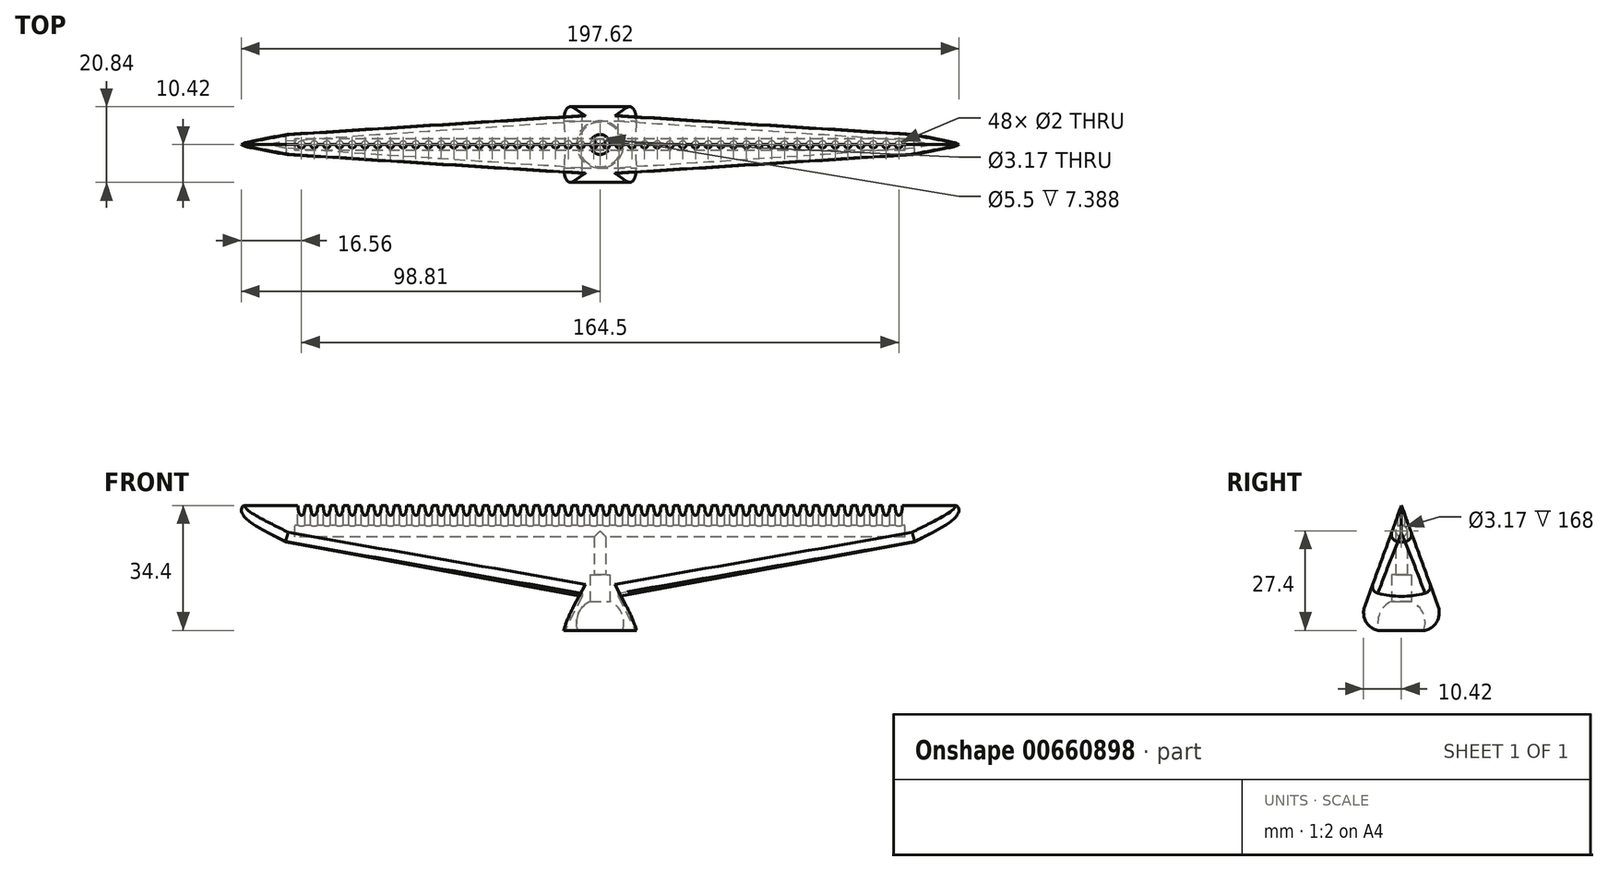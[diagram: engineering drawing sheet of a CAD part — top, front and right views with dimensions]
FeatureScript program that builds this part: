
annotation { "Feature Type Name" : "Feature", "Feature Type Description" : "" }
export const myFeature = defineFeature(function(context is Context, id is Id, definition is map)
    precondition{}
    {
        {
            var Q0;
            Q0=qCreatedBy(makeId("Front.planeOp"),FACE);
            var sketch = newSketch(context, id + "F0", { "sketchPlane" : qUnion([Q0])});
            skLineSegment(sketch, "E0.MirrorCS", {"start": v(10, 0) * mm, "end": v(5, 10) * mm});
            skLineSegment(sketch, "E1.MirrorCS", {"start": v(86.5, 25) * mm, "end": v(5, 10) * mm});
            skLineSegment(sketch, "E2.MirrorCS", {"start": v(0, 0) * mm, "end": v(10, 0) * mm});
            skLineSegment(sketch, "E3", {"start": v(0, 35) * mm, "end": v(100, 35) * mm});
            skPoint(sketch, "E4.end.orphan", {"position": v(0, 30) * mm});
            skArc(sketch, "E5", {"start": v(99.82, 31.74) * mm, "mid": v(100.91, 33.31) * mm, "end": v(100, 35) * mm});
            skPoint(sketch, "E5.second.point", {"position": v(98.3, 31.76) * mm});
            skPoint(sketch, "E5.third.point", {"position": v(100, 31.83) * mm});
            skLineSegment(sketch, "E6", {"start": v(86.5, 25) * mm, "end": v(100, 31.83) * mm});
            skArc(sketch, "E7.MirrorCS", {"start": v(-99.82, 31.74) * mm, "mid": v(-100.91, 33.31) * mm, "end": v(-100, 35) * mm});
            skLineSegment(sketch, "E8.MirrorCS", {"start": v(0, 35) * mm, "end": v(-100, 35) * mm});
            skLineSegment(sketch, "E9.MirrorCS", {"start": v(0, 0) * mm, "end": v(-10, 0) * mm});
            skPoint(sketch, "E10.MirrorP", {"position": v(-100, 31.83) * mm});
            skLineSegment(sketch, "E11.MirrorCS", {"start": v(-86.5, 25) * mm, "end": v(-5, 10) * mm});
            skLineSegment(sketch, "E12.MirrorCS", {"start": v(-10, 0) * mm, "end": v(-5, 10) * mm});
            skPoint(sketch, "E13.MirrorP", {"position": v(-98.3, 31.76) * mm});
            skLineSegment(sketch, "E14.MirrorCS", {"start": v(-86.5, 25) * mm, "end": v(-100, 31.83) * mm});
            skPoint(sketch, "E15.orphan", {"position": v(0, 0) * mm});
            skSolve(sketch);
        }
        {
            var Q0;
            Q0=makeQuery(id+"F0.imprint","IMPRINT",FACE,{"disambiguationData":[TD([[makeQuery(id+"F0.imprint","IMPRINT",EDGE,{"derivedFrom":sQuery(id+"F0.wireOp",EDGE,"E0.MirrorCS")}),1.0]])]});
            var Q1;
            Q1=sQuery(id+"F0.wireOp",EDGE,"E8.MirrorCS");
            revolve(context, id + "F1", {"entities" : qUnion([Q0]), "axis" : qUnion([Q1]), "revolveType" : RevolveType.SYMMETRIC, "angle" : 40 * degree});
        }
        {
            var Q0;
            Q0=qCreatedBy(makeId("Right.planeOp"),FACE);
            var sketch = newSketch(context, id + "F2", { "sketchPlane" : qUnion([Q0])});
            skLineSegment(sketch, "E16", {"start": v(0, 0.6) * mm, "end": v(-10, 0.6) * mm});
            skLineSegment(sketch, "E17", {"start": v(0, 0) * mm, "end": v(-10, 0) * mm});
            skLineSegment(sketch, "E18", {"start": v(-10, 0.6) * mm, "end": v(-10, 0) * mm});
            skLineSegment(sketch, "E19.MirrorCS", {"start": v(0, 0.6) * mm, "end": v(10, 0.6) * mm});
            skLineSegment(sketch, "E20.MirrorCS", {"start": v(10, 0.6) * mm, "end": v(10, 0) * mm});
            skLineSegment(sketch, "E21.MirrorCS", {"start": v(0, 0) * mm, "end": v(10, 0) * mm});
            skSolve(sketch);
        }
        {
            var Q0;
            Q0=makeQuery(id+"F2.imprint","IMPRINT",FACE,{"disambiguationData":[TD([[makeQuery(id+"F2.imprint","IMPRINT",EDGE,{"derivedFrom":sQuery(id+"F2.wireOp",EDGE,"E16")}),1.0]])]});
            extrude(context, id + "F3", {"entities" : qUnion([Q0]), "operationType" : NewBodyOperationType.REMOVE, "endBound" : BoundingType.SYMMETRIC, "depth" : 20 * mm, "offsetDistance" : 25 * mm});
        }
        {
            var Q0;
            Q0=qCreatedBy(makeId("Front.planeOp"),FACE);
            var sketch = newSketch(context, id + "F4", { "sketchPlane" : qUnion([Q0])});
            skLineSegment(sketch, "E22", {"start": v(0, 0) * mm, "end": v(0, 1.02) * mm});
            skLineSegment(sketch, "E23", {"start": v(0, 1.02) * mm, "end": v(0, 2.72) * mm});
            skArc(sketch, "E24", {"start": v(0, 9.22) * mm, "mid": v(-6.5, 2.72) * mm, "end": v(0, -3.78) * mm});
            skLineSegment(sketch, "E25", {"start": v(0, 0) * mm, "end": v(0, -3.78) * mm});
            skLineSegment(sketch, "E26", {"start": v(0, 2.72) * mm, "end": v(0, 9.22) * mm});
            skSolve(sketch);
        }
        {
            var Q0;
            Q0=makeQuery(id+"F4.imprint","IMPRINT",FACE,{"disambiguationData":[TD([[makeQuery(id+"F4.imprint","IMPRINT",EDGE,{"derivedFrom":sQuery(id+"F4.wireOp",EDGE,"E22")}),1.0]])]});
            var Q1;
            Q1=sQuery(id+"F4.wireOp",EDGE,"E22");
            revolve(context, id + "F5", {"operationType" : NewBodyOperationType.REMOVE, "entities" : qUnion([Q0]), "axis" : qUnion([Q1]), "revolveType" : RevolveType.FULL, "oppositeDirection" : true});
        }
        {
            var Q0;
            Q0=qCreatedBy(makeId("Top.planeOp"),FACE);
            var sketch = newSketch(context, id + "F6", { "sketchPlane" : qUnion([Q0])});
            skCircle(sketch, "E27", {"center": v(0, 0) * mm, "radius": 1.59 * mm});
            skSolve(sketch);
        }
        {
            var Q0;
            Q0=makeQuery(id+"F6.imprint","IMPRINT",FACE,{"disambiguationData":[TD([[makeQuery(id+"F6.imprint","IMPRINT",EDGE,{"derivedFrom":sQuery(id+"F6.wireOp",EDGE,"E27")}),1.0]])]});
            extrude(context, id + "F7", {"entities" : qUnion([Q0]), "operationType" : NewBodyOperationType.REMOVE, "depth" : 28 * mm, "offsetDistance" : 25 * mm});
        }
        {
            var Q0;
            Q0=qCreatedBy(makeId("Right.planeOp"),FACE);
            var sketch = newSketch(context, id + "F8", { "sketchPlane" : qUnion([Q0])});
            skLineSegment(sketch, "E28", {"start": v(0, 0) * mm, "end": v(0, 28) * mm});
            skCircle(sketch, "E29", {"center": v(0, 28) * mm, "radius": 1.59 * mm});
            skSolve(sketch);
        }
        {
            var Q0;
            Q0 = qSketchRegion(id + "F8", true);
            extrude(context, id + "F9", {"entities" : qUnion([Q0]), "operationType" : NewBodyOperationType.REMOVE, "endBound" : BoundingType.SYMMETRIC, "depth" : 168 * mm, "offsetDistance" : 25 * mm});
        }
        {
            var Q0;
            Q0=qCreatedBy(makeId("Top.planeOp"),FACE);
            cPlane(context, id + "F10", {"entities" : qUnion([Q0]), "cplaneType" : CPlaneType.OFFSET, "offset" : 35 * mm, "width" : 150 * mm, "height" : 150 * mm});
        }
        {
            var Q0;
            Q0=qCreatedBy(id+"F10.planeOp",FACE);
            var sketch = newSketch(context, id + "F11", { "sketchPlane" : qUnion([Q0])});
            skLineSegment(sketch, "E30", {"start": v(0, 0) * mm, "end": v(1.75, 0) * mm});
            skLineSegment(sketch, "E31", {"start": v(1.75, 0) * mm, "end": v(5.25, 0) * mm});
            skLineSegment(sketch, "E32", {"start": v(5.25, 0) * mm, "end": v(8.75, 0) * mm});
            skLineSegment(sketch, "E33", {"start": v(8.75, 0) * mm, "end": v(12.25, 0) * mm});
            skLineSegment(sketch, "E34", {"start": v(12.25, 0) * mm, "end": v(15.75, 0) * mm});
            skLineSegment(sketch, "E35", {"start": v(15.75, 0) * mm, "end": v(19.25, 0) * mm});
            skLineSegment(sketch, "E36", {"start": v(19.25, 0) * mm, "end": v(22.75, 0) * mm});
            skLineSegment(sketch, "E37", {"start": v(22.75, 0) * mm, "end": v(26.25, 0) * mm});
            skLineSegment(sketch, "E38", {"start": v(26.25, 0) * mm, "end": v(29.75, 0) * mm});
            skLineSegment(sketch, "E39", {"start": v(29.75, 0) * mm, "end": v(33.25, 0) * mm});
            skLineSegment(sketch, "E40", {"start": v(33.25, 0) * mm, "end": v(36.75, 0) * mm});
            skLineSegment(sketch, "E41", {"start": v(36.75, 0) * mm, "end": v(40.25, 0) * mm});
            skLineSegment(sketch, "E42", {"start": v(40.25, 0) * mm, "end": v(43.75, 0) * mm});
            skLineSegment(sketch, "E43", {"start": v(43.75, 0) * mm, "end": v(47.25, 0) * mm});
            skLineSegment(sketch, "E44", {"start": v(47.25, 0) * mm, "end": v(50.75, 0) * mm});
            skLineSegment(sketch, "E45", {"start": v(50.75, 0) * mm, "end": v(54.25, 0) * mm});
            skLineSegment(sketch, "E46", {"start": v(54.25, 0) * mm, "end": v(57.75, 0) * mm});
            skLineSegment(sketch, "E47", {"start": v(57.75, 0) * mm, "end": v(61.25, 0) * mm});
            skLineSegment(sketch, "E48", {"start": v(61.25, 0) * mm, "end": v(64.75, 0) * mm});
            skLineSegment(sketch, "E49", {"start": v(64.75, 0) * mm, "end": v(68.25, 0) * mm});
            skLineSegment(sketch, "E50", {"start": v(68.25, 0) * mm, "end": v(71.75, 0) * mm});
            skLineSegment(sketch, "E51", {"start": v(71.75, 0) * mm, "end": v(75.25, 0) * mm});
            skLineSegment(sketch, "E52", {"start": v(75.25, 0) * mm, "end": v(78.75, 0) * mm});
            skLineSegment(sketch, "E53", {"start": v(78.75, 0) * mm, "end": v(82.25, 0) * mm});
            skLineSegment(sketch, "E54", {"start": v(82.25, 0) * mm, "end": v(85.75, 0) * mm});
            skLineSegment(sketch, "E55.MirrorCS", {"start": v(-47.25, 0) * mm, "end": v(-50.75, 0) * mm});
            skLineSegment(sketch, "E56.MirrorCS", {"start": v(-43.75, 0) * mm, "end": v(-47.25, 0) * mm});
            skLineSegment(sketch, "E57.MirrorCS", {"start": v(-61.25, 0) * mm, "end": v(-64.75, 0) * mm});
            skLineSegment(sketch, "E58.MirrorCS", {"start": v(-57.75, 0) * mm, "end": v(-61.25, 0) * mm});
            skLineSegment(sketch, "E59.MirrorCS", {"start": v(-64.75, 0) * mm, "end": v(-68.25, 0) * mm});
            skLineSegment(sketch, "E60.MirrorCS", {"start": v(-78.75, 0) * mm, "end": v(-82.25, 0) * mm});
            skLineSegment(sketch, "E61.MirrorCS", {"start": v(-54.25, 0) * mm, "end": v(-57.75, 0) * mm});
            skLineSegment(sketch, "E62.MirrorCS", {"start": v(-40.25, 0) * mm, "end": v(-43.75, 0) * mm});
            skLineSegment(sketch, "E63.MirrorCS", {"start": v(-36.75, 0) * mm, "end": v(-40.25, 0) * mm});
            skLineSegment(sketch, "E64.MirrorCS", {"start": v(-33.25, 0) * mm, "end": v(-36.75, 0) * mm});
            skLineSegment(sketch, "E65.MirrorCS", {"start": v(-50.75, 0) * mm, "end": v(-54.25, 0) * mm});
            skLineSegment(sketch, "E66.MirrorCS", {"start": v(-1.75, 0) * mm, "end": v(-5.25, 0) * mm});
            skLineSegment(sketch, "E67.MirrorCS", {"start": v(-19.25, 0) * mm, "end": v(-22.75, 0) * mm});
            skLineSegment(sketch, "E68.MirrorCS", {"start": v(-15.75, 0) * mm, "end": v(-19.25, 0) * mm});
            skLineSegment(sketch, "E69.MirrorCS", {"start": v(-68.25, 0) * mm, "end": v(-71.75, 0) * mm});
            skLineSegment(sketch, "E70.MirrorCS", {"start": v(0, 0) * mm, "end": v(-1.75, 0) * mm});
            skLineSegment(sketch, "E71.MirrorCS", {"start": v(-5.25, 0) * mm, "end": v(-8.75, 0) * mm});
            skLineSegment(sketch, "E72.MirrorCS", {"start": v(-29.75, 0) * mm, "end": v(-33.25, 0) * mm});
            skLineSegment(sketch, "E73.MirrorCS", {"start": v(-22.75, 0) * mm, "end": v(-26.25, 0) * mm});
            skLineSegment(sketch, "E74.MirrorCS", {"start": v(-26.25, 0) * mm, "end": v(-29.75, 0) * mm});
            skLineSegment(sketch, "E75.MirrorCS", {"start": v(-12.25, 0) * mm, "end": v(-15.75, 0) * mm});
            skLineSegment(sketch, "E76.MirrorCS", {"start": v(-71.75, 0) * mm, "end": v(-75.25, 0) * mm});
            skLineSegment(sketch, "E77.MirrorCS", {"start": v(-75.25, 0) * mm, "end": v(-78.75, 0) * mm});
            skLineSegment(sketch, "E78.MirrorCS", {"start": v(-8.75, 0) * mm, "end": v(-12.25, 0) * mm});
            skLineSegment(sketch, "E79.MirrorCS", {"start": v(-82.25, 0) * mm, "end": v(-85.75, 0) * mm});
            skSolve(sketch);
        }
        {
            var Q0;
            Q0=sQuery(id+"F11.wireOp",VERTEX,"E60.MirrorCS.end");
            var Q1;
            Q1=sQuery(id+"F11.wireOp",VERTEX,"E77.MirrorCS.end");
            var Q2;
            Q2=sQuery(id+"F11.wireOp",VERTEX,"E76.MirrorCS.end");
            var Q3;
            Q3=sQuery(id+"F11.wireOp",VERTEX,"E69.MirrorCS.end");
            var Q4;
            Q4=sQuery(id+"F11.wireOp",VERTEX,"E59.MirrorCS.end");
            var Q5;
            Q5=sQuery(id+"F11.wireOp",VERTEX,"E57.MirrorCS.end");
            var Q6;
            Q6=sQuery(id+"F11.wireOp",VERTEX,"E58.MirrorCS.end");
            var Q7;
            Q7=sQuery(id+"F11.wireOp",VERTEX,"E61.MirrorCS.end");
            var Q8;
            Q8=sQuery(id+"F11.wireOp",VERTEX,"E65.MirrorCS.end");
            var Q9;
            Q9=sQuery(id+"F11.wireOp",VERTEX,"E55.MirrorCS.end");
            var Q10;
            Q10=sQuery(id+"F11.wireOp",VERTEX,"E55.MirrorCS.start");
            var Q11;
            Q11=sQuery(id+"F11.wireOp",VERTEX,"E56.MirrorCS.start");
            var Q12;
            Q12=sQuery(id+"F11.wireOp",VERTEX,"E62.MirrorCS.start");
            var Q13;
            Q13=sQuery(id+"F11.wireOp",VERTEX,"E63.MirrorCS.start");
            var Q14;
            Q14=sQuery(id+"F11.wireOp",VERTEX,"E64.MirrorCS.start");
            var Q15;
            Q15=sQuery(id+"F11.wireOp",VERTEX,"E72.MirrorCS.start");
            var Q16;
            Q16=sQuery(id+"F11.wireOp",VERTEX,"E73.MirrorCS.end");
            var Q17;
            Q17=sQuery(id+"F11.wireOp",VERTEX,"E67.MirrorCS.end");
            var Q18;
            Q18=sQuery(id+"F11.wireOp",VERTEX,"E68.MirrorCS.end");
            var Q19;
            Q19=sQuery(id+"F11.wireOp",VERTEX,"E75.MirrorCS.end");
            var Q20;
            Q20=sQuery(id+"F11.wireOp",VERTEX,"E75.MirrorCS.start");
            var Q21;
            Q21=sQuery(id+"F11.wireOp",VERTEX,"E78.MirrorCS.start");
            var Q22;
            Q22=sQuery(id+"F11.wireOp",VERTEX,"E71.MirrorCS.start");
            var Q23;
            Q23=sQuery(id+"F11.wireOp",VERTEX,"E70.MirrorCS.end");
            var Q24;
            Q24=sQuery(id+"F11.wireOp",VERTEX,"E31.start");
            var Q25;
            Q25=sQuery(id+"F11.wireOp",VERTEX,"E32.start");
            var Q26;
            Q26=sQuery(id+"F11.wireOp",VERTEX,"E33.start");
            var Q27;
            Q27=sQuery(id+"F11.wireOp",VERTEX,"E34.start");
            var Q28;
            Q28=sQuery(id+"F11.wireOp",VERTEX,"E35.start");
            var Q29;
            Q29=sQuery(id+"F11.wireOp",VERTEX,"E36.start");
            var Q30;
            Q30=sQuery(id+"F11.wireOp",VERTEX,"E37.start");
            var Q31;
            Q31=sQuery(id+"F11.wireOp",VERTEX,"E38.start");
            var Q32;
            Q32=sQuery(id+"F11.wireOp",VERTEX,"E39.start");
            var Q33;
            Q33=sQuery(id+"F11.wireOp",VERTEX,"E40.start");
            var Q34;
            Q34=sQuery(id+"F11.wireOp",VERTEX,"E41.start");
            var Q35;
            Q35=sQuery(id+"F11.wireOp",VERTEX,"E41.end");
            var Q36;
            Q36=sQuery(id+"F11.wireOp",VERTEX,"E43.start");
            var Q37;
            Q37=sQuery(id+"F11.wireOp",VERTEX,"E43.end");
            var Q38;
            Q38=sQuery(id+"F11.wireOp",VERTEX,"E44.end");
            var Q39;
            Q39=sQuery(id+"F11.wireOp",VERTEX,"E46.start");
            var Q40;
            Q40=sQuery(id+"F11.wireOp",VERTEX,"E47.start");
            var Q41;
            Q41=sQuery(id+"F11.wireOp",VERTEX,"E48.start");
            var Q42;
            Q42=sQuery(id+"F11.wireOp",VERTEX,"E49.start");
            var Q43;
            Q43=sQuery(id+"F11.wireOp",VERTEX,"E49.end");
            var Q44;
            Q44=sQuery(id+"F11.wireOp",VERTEX,"E51.start");
            var Q45;
            Q45=sQuery(id+"F11.wireOp",VERTEX,"E51.end");
            var Q46;
            Q46=sQuery(id+"F11.wireOp",VERTEX,"E52.end");
            var Q47;
            Q47=sQuery(id+"F11.wireOp",VERTEX,"E54.start");
            var Q48;
            Q48=makeQuery(id+"F1.opRevolve","SWEPT_BODY",BODY,{"disambiguationData":[OSD([sQuery(id+"F0.wireOp",EDGE,"E0.MirrorCS"),sQuery(id+"F0.wireOp",EDGE,"E1.MirrorCS"),sQuery(id+"F0.wireOp",EDGE,"E2.MirrorCS"),sQuery(id+"F0.wireOp",EDGE,"E3"),sQuery(id+"F0.wireOp",EDGE,"E5"),sQuery(id+"F0.wireOp",EDGE,"E6"),sQuery(id+"F0.wireOp",EDGE,"E7.MirrorCS"),sQuery(id+"F0.wireOp",EDGE,"E8.MirrorCS"),sQuery(id+"F0.wireOp",EDGE,"E9.MirrorCS"),sQuery(id+"F0.wireOp",EDGE,"E11.MirrorCS"),sQuery(id+"F0.wireOp",EDGE,"E12.MirrorCS"),sQuery(id+"F0.wireOp",EDGE,"E14.MirrorCS")])]});
            hole(context, id + "F12", {"style" : HoleStyle.SIMPLE, "endStyle" : HoleEndStyle.BLIND, "holeDiameter" : 2 * mm, "majorDiameter" : 5 * mm, "holeDepth" : 5 * mm, "isTappedThrough" : true, "tappedDepth" : 12 * mm, "tapClearance" : 3, "locations" : qUnion([Q0, Q1, Q2, Q3, Q4, Q5, Q6, Q7, Q8, Q9, Q10, Q11, Q12, Q13, Q14, Q15, Q16, Q17, Q18, Q19, Q20, Q21, Q22, Q23, Q24, Q25, Q26, Q27, Q28, Q29, Q30, Q31, Q32, Q33, Q34, Q35, Q36, Q37, Q38, Q39, Q40, Q41, Q42, Q43, Q44, Q45, Q46, Q47]), "scope" : qUnion([Q48])});
        }
        {
            var Q0;
            Q0=qCreatedBy(makeId("Top.planeOp"),FACE);
            var sketch = newSketch(context, id + "F13", { "sketchPlane" : qUnion([Q0])});
            skCircle(sketch, "E80", {"center": v(0, 0) * mm, "radius": 2.75 * mm});
            skSolve(sketch);
        }
        {
            var Q0;
            Q0=makeQuery(id+"F13.imprint","IMPRINT",FACE,{"disambiguationData":[TD([[makeQuery(id+"F13.imprint","IMPRINT",EDGE,{"derivedFrom":sQuery(id+"F13.wireOp",EDGE,"E80")}),1.0]])]});
            extrude(context, id + "F14", {"entities" : qUnion([Q0]), "operationType" : NewBodyOperationType.REMOVE, "depth" : 16 * mm, "offsetDistance" : 25 * mm});
        }
        {
            var Q0;
            Q0=makeQuery(id+"F1.opRevolve","CAP_EDGE",EDGE,{"disambiguationData":[OSD([sQuery(id+"F0.wireOp",EDGE,"E2.MirrorCS"),sQuery(id+"F0.wireOp",EDGE,"E9.MirrorCS")])],"isStart":false});
            var Q1;
            Q1=makeQuery(id+"F1.opRevolve","CAP_EDGE",EDGE,{"disambiguationData":[OSD([sQuery(id+"F0.wireOp",EDGE,"E2.MirrorCS"),sQuery(id+"F0.wireOp",EDGE,"E9.MirrorCS")])],"isStart":true});
            fillet(context, id + "F15", {"entities" : qUnion([Q0, Q1]), "radius" : 5 * mm, "tangentPropagation" : true, "allowEdgeOverflow" : false});
        }
        {
            var Q0;
            Q0=makeQuery(id+"F1.opRevolve","CAP_EDGE",EDGE,{"disambiguationData":[OSD([sQuery(id+"F0.wireOp",EDGE,"E1.MirrorCS")])],"isStart":false});
            var Q1;
            Q1=makeQuery(id+"F1.opRevolve","CAP_EDGE",EDGE,{"disambiguationData":[OSD([sQuery(id+"F0.wireOp",EDGE,"E11.MirrorCS")])],"isStart":false});
            var Q2;
            Q2=makeQuery(id+"F1.opRevolve","CAP_EDGE",EDGE,{"disambiguationData":[OSD([sQuery(id+"F0.wireOp",EDGE,"E11.MirrorCS")])],"isStart":true});
            var Q3;
            Q3=makeQuery(id+"F1.opRevolve","CAP_EDGE",EDGE,{"disambiguationData":[OSD([sQuery(id+"F0.wireOp",EDGE,"E1.MirrorCS")])],"isStart":true});
            var Q4;
            Q4=makeQuery(id+"F1.opRevolve","CAP_EDGE",EDGE,{"disambiguationData":[OSD([sQuery(id+"F0.wireOp",EDGE,"E14.MirrorCS")])],"isStart":false});
            var Q5;
            Q5=makeQuery(id+"F1.opRevolve","CAP_EDGE",EDGE,{"disambiguationData":[OSD([sQuery(id+"F0.wireOp",EDGE,"E14.MirrorCS")])],"isStart":true});
            var Q6;
            Q6=makeQuery(id+"F1.opRevolve","CAP_EDGE",EDGE,{"disambiguationData":[OSD([sQuery(id+"F0.wireOp",EDGE,"E6")])],"isStart":false});
            var Q7;
            Q7=makeQuery(id+"F1.opRevolve","CAP_EDGE",EDGE,{"disambiguationData":[OSD([sQuery(id+"F0.wireOp",EDGE,"E6")])],"isStart":true});
            fillet(context, id + "F16", {"entities" : qUnion([Q0, Q1, Q2, Q3, Q4, Q5, Q6, Q7]), "radius" : 2 * mm, "tangentPropagation" : true, "allowEdgeOverflow" : false});
        }
    });
